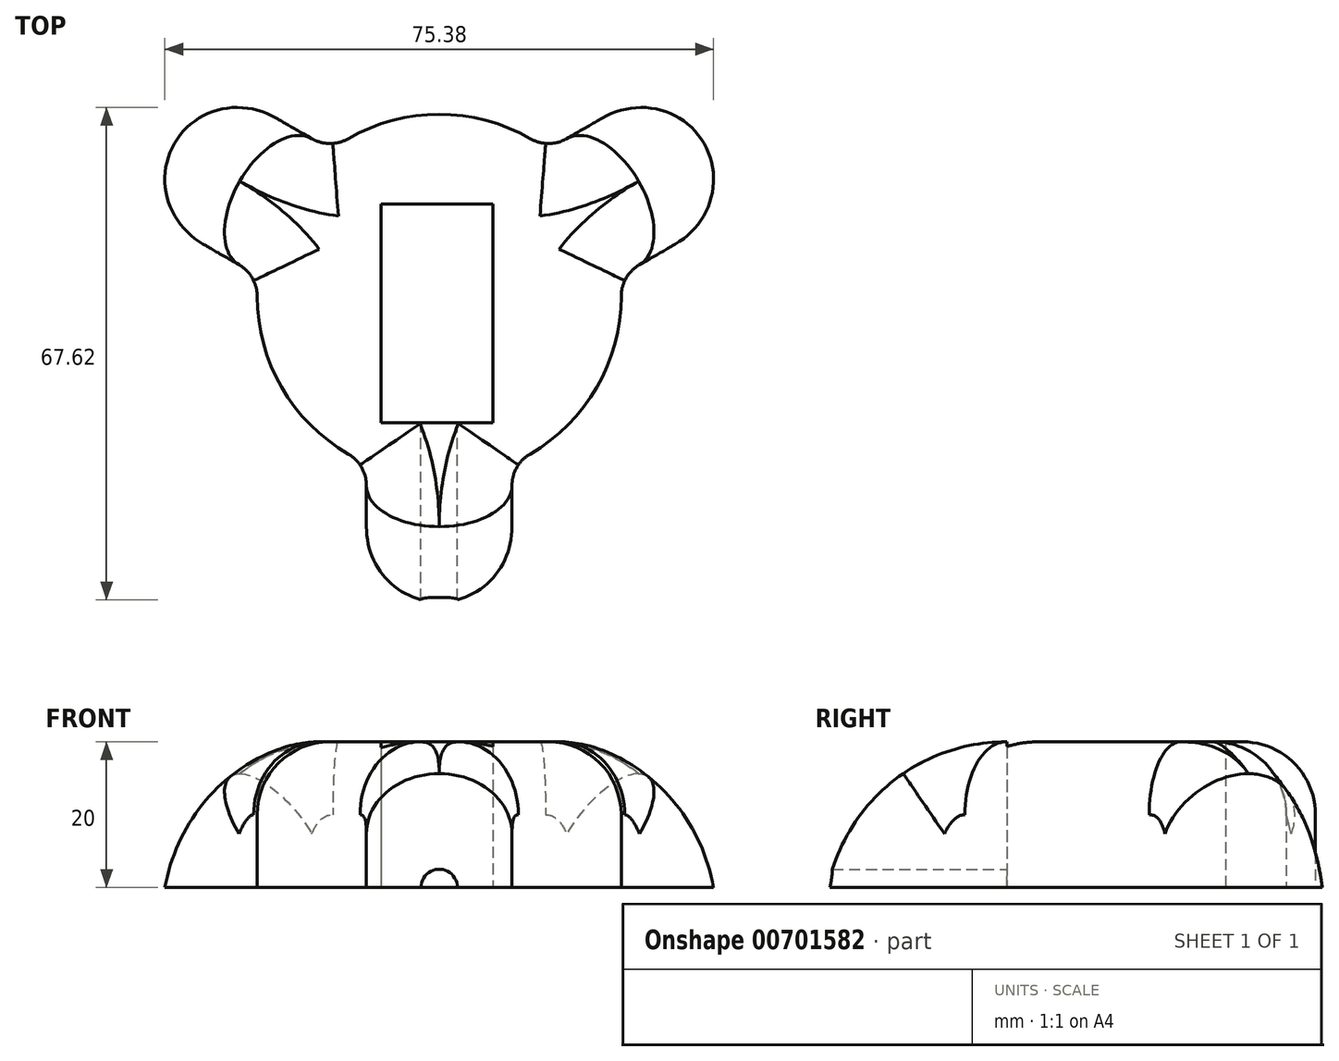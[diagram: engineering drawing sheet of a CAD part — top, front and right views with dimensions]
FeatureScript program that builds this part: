
annotation { "Feature Type Name" : "Feature", "Feature Type Description" : "" }
export const myFeature = defineFeature(function(context is Context, id is Id, definition is map)
    precondition{}
    {
        {
            var Q0;
            Q0=qCreatedBy(makeId("Top.planeOp"),FACE);
            var sketch = newSketch(context, id + "F0", { "sketchPlane" : qUnion([Q0])});
            skCircle(sketch, "E0", {"center": v(0, 0) * mm, "radius": 25 * mm});
            skSolve(sketch);
        }
        {
            var Q0;
            Q0=makeQuery(id+"F0.imprint","IMPRINT",FACE,{"disambiguationData":[TD([[makeQuery(id+"F0.imprint","IMPRINT",EDGE,{"derivedFrom":sQuery(id+"F0.wireOp",EDGE,"E0")}),1.0]])]});
            extrude(context, id + "F1", {"entities" : qUnion([Q0]), "depth" : 20 * mm, "offsetDistance" : 25 * mm});
        }
        {
            var Q0;
            Q0=qCreatedBy(makeId("Top.planeOp"),FACE);
            var sketch = newSketch(context, id + "F2", { "sketchPlane" : qUnion([Q0])});
            skLineSegment(sketch, "E1.bottom", {"start": v(-10, 0) * mm, "end": v(10, 0) * mm});
            skLineSegment(sketch, "E1.top", {"start": v(-10, -42) * mm, "end": v(10, -42) * mm});
            skLineSegment(sketch, "E1.left", {"start": v(-10, 0) * mm, "end": v(-10, -42) * mm});
            skLineSegment(sketch, "E1.right", {"start": v(10, 0) * mm, "end": v(10, -42) * mm});
            skSolve(sketch);
        }
        {
            var Q0;
            Q0=makeQuery(id+"F2.imprint","IMPRINT",FACE,{"disambiguationData":[TD([[makeQuery(id+"F2.imprint","IMPRINT",EDGE,{"derivedFrom":sQuery(id+"F2.wireOp",EDGE,"E1.bottom")}),-1.0]])]});
            extrude(context, id + "F3", {"entities" : qUnion([Q0]), "operationType" : NewBodyOperationType.ADD, "depth" : 20 * mm, "offsetDistance" : 25 * mm});
        }
        {
            var Q0;
            Q0=qCreatedBy(makeId("Right.planeOp"),FACE);
            var sketch = newSketch(context, id + "F4", { "sketchPlane" : qUnion([Q0])});
            skLineSegment(sketch, "E2", {"start": v(0, 74.5) * mm, "end": v(0, 0) * mm});
            skSolve(sketch);
        }
        {
            var Q0;
            Q0=makeQuery(id+"F1.opExtrude","SWEPT_BODY",BODY,{"disambiguationData":[OSD([sQuery(id+"F0.wireOp",EDGE,"E0")])]});
            var Q1;
            Q1=sQuery(id+"F4.wireOp",EDGE,"E2");
            circularPattern(context, id + "F5", {"entities" : qUnion([Q0]), "axis" : qUnion([Q1]), "angle" : 360 * degree, "instanceCount" : 3, "equalSpace" : true});
        }
        {
            var Q0;
            Q0=makeQuery(id+"F5.opPattern","COPY",BODY,{"derivedFrom":makeQuery(id+"F1.opExtrude","SWEPT_BODY",BODY,{"disambiguationData":[OSD([sQuery(id+"F0.wireOp",EDGE,"E0")])]}),"instanceName":"1"});
            var Q1;
            Q1=makeQuery(id+"F1.opExtrude","SWEPT_BODY",BODY,{"disambiguationData":[OSD([sQuery(id+"F0.wireOp",EDGE,"E0")])]});
            var Q2;
            Q2=makeQuery(id+"F5.opPattern","COPY",BODY,{"derivedFrom":makeQuery(id+"F1.opExtrude","SWEPT_BODY",BODY,{"disambiguationData":[OSD([sQuery(id+"F0.wireOp",EDGE,"E0")])]}),"instanceName":"2"});
            booleanBodies(context, id + "F6", {"operationType" : BooleanOperationType.UNION, "tools" : qUnion([Q0, Q1, Q2])});
        }
        {
            var Q0;
            Q0=makeQuery(id+"F3.opExtrude","CAP_EDGE",EDGE,{"disambiguationData":[OSD([sQuery(id+"F2.wireOp",EDGE,"E1.top")])],"isStart":false});
            var Q1;
            Q1=makeQuery(id+"F5.opPattern","COPY",EDGE,{"derivedFrom":makeQuery(id+"F3.opExtrude","CAP_EDGE",EDGE,{"disambiguationData":[OSD([sQuery(id+"F2.wireOp",EDGE,"E1.top")])],"isStart":false}),"instanceName":"1"});
            var Q2;
            Q2=makeQuery(id+"F5.opPattern","COPY",EDGE,{"derivedFrom":makeQuery(id+"F3.opExtrude","CAP_EDGE",EDGE,{"disambiguationData":[OSD([sQuery(id+"F2.wireOp",EDGE,"E1.top")])],"isStart":false}),"instanceName":"2"});
            fillet(context, id + "F7", {"entities" : qUnion([Q0, Q1, Q2]), "radius" : 25 * mm, "tangentPropagation" : true, "allowEdgeOverflow" : false});
        }
        {
            var Q0;
            Q0=makeQuery(id+"F5.opPattern","COPY",EDGE,{"derivedFrom":makeQuery(id+"F3.boolean.opBoolean","INTERSECT",EDGE,{"derivedFrom":[makeQuery(id+"F1.opExtrude","SWEPT_FACE",FACE,{"disambiguationData":[OSD([sQuery(id+"F0.wireOp",EDGE,"E0")])]}),makeQuery(id+"F3.opExtrude","SWEPT_FACE",FACE,{"disambiguationData":[OSD([sQuery(id+"F2.wireOp",EDGE,"E1.right")])]})]}),"instanceName":"1"});
            var Q1;
            {var subQ0=makeQuery(id+"F1.opExtrude","SWEPT_FACE",FACE,{"disambiguationData":[OSD([sQuery(id+"F0.wireOp",EDGE,"E0")])]});var subQ1=makeQuery(id+"F5.opPattern","COPY",FACE,{"derivedFrom":subQ0,"instanceName":"1"});Q1=makeQuery(id+"F6.opBoolean","INTERSECT",EDGE,{"disambiguationData":[topologyDisambiguationEdgeConnected([makeQuery(id+"F3.opExtrude","SWEPT_FACE",FACE,{"disambiguationData":[OSD([sQuery(id+"F2.wireOp",EDGE,"E1.left")])]})])],"derivedFrom":[subQ1,makeQuery(id+"F5.opPattern","COPY",FACE,{"derivedFrom":subQ0,"instanceName":"2"})]});}
            var Q2;
            Q2=makeQuery(id+"F5.opPattern","COPY",EDGE,{"derivedFrom":makeQuery(id+"F3.boolean.opBoolean","INTERSECT",EDGE,{"derivedFrom":[makeQuery(id+"F1.opExtrude","SWEPT_FACE",FACE,{"disambiguationData":[OSD([sQuery(id+"F0.wireOp",EDGE,"E0")])]}),makeQuery(id+"F3.opExtrude","SWEPT_FACE",FACE,{"disambiguationData":[OSD([sQuery(id+"F2.wireOp",EDGE,"E1.left")])]})]}),"instanceName":"1"});
            var Q3;
            {var subQ0=makeQuery(id+"F1.opExtrude","SWEPT_FACE",FACE,{"disambiguationData":[OSD([sQuery(id+"F0.wireOp",EDGE,"E0")])]});var subQ1=makeQuery(id+"F5.opPattern","COPY",FACE,{"derivedFrom":subQ0,"instanceName":"1"});Q3=makeQuery(id+"F6.opBoolean","INTERSECT",EDGE,{"disambiguationData":[topologyDisambiguationEdgeConnected([makeQuery(id+"F5.opPattern","COPY",FACE,{"derivedFrom":makeQuery(id+"F3.opExtrude","SWEPT_FACE",FACE,{"disambiguationData":[OSD([sQuery(id+"F2.wireOp",EDGE,"E1.right")])]}),"instanceName":"2"})])],"derivedFrom":[subQ0,subQ1]});}
            var Q4;
            {var subQ0=makeQuery(id+"F1.opExtrude","SWEPT_FACE",FACE,{"disambiguationData":[OSD([sQuery(id+"F0.wireOp",EDGE,"E0")])]});var subQ1=makeQuery(id+"F5.opPattern","COPY",FACE,{"derivedFrom":subQ0,"instanceName":"1"});Q4=makeQuery(id+"F6.opBoolean","INTERSECT",EDGE,{"disambiguationData":[topologyDisambiguationEdgeConnected([makeQuery(id+"F5.opPattern","COPY",FACE,{"derivedFrom":makeQuery(id+"F3.opExtrude","SWEPT_FACE",FACE,{"disambiguationData":[OSD([sQuery(id+"F2.wireOp",EDGE,"E1.left")])]}),"instanceName":"2"})])],"derivedFrom":[subQ0,subQ1]});}
            var Q5;
            {var subQ0=makeQuery(id+"F1.opExtrude","SWEPT_FACE",FACE,{"disambiguationData":[OSD([sQuery(id+"F0.wireOp",EDGE,"E0")])]});var subQ1=makeQuery(id+"F5.opPattern","COPY",FACE,{"derivedFrom":subQ0,"instanceName":"1"});Q5=makeQuery(id+"F6.opBoolean","INTERSECT",EDGE,{"disambiguationData":[topologyDisambiguationEdgeConnected([makeQuery(id+"F3.opExtrude","SWEPT_FACE",FACE,{"disambiguationData":[OSD([sQuery(id+"F2.wireOp",EDGE,"E1.right")])]})])],"derivedFrom":[subQ1,makeQuery(id+"F5.opPattern","COPY",FACE,{"derivedFrom":subQ0,"instanceName":"2"})]});}
            fillet(context, id + "F8", {"entities" : qUnion([Q0, Q1, Q2, Q3, Q4, Q5]), "radius" : 5 * mm, "tangentPropagation" : true, "allowEdgeOverflow" : false});
        }
        {
            var Q0;
            Q0=makeQuery(id+"F7.opFillet","BLEND_EDGE",EDGE,{"blendedFrom":[makeQuery(id+"F5.opPattern","COPY",EDGE,{"derivedFrom":makeQuery(id+"F3.opExtrude","CAP_EDGE",EDGE,{"disambiguationData":[OSD([sQuery(id+"F2.wireOp",EDGE,"E1.top")])],"isStart":false}),"instanceName":"1"}),makeQuery(id+"F5.opPattern","COPY",FACE,{"derivedFrom":makeQuery(id+"F3.opExtrude","SWEPT_FACE",FACE,{"disambiguationData":[OSD([sQuery(id+"F2.wireOp",EDGE,"E1.right")])]}),"instanceName":"1"})],"blendedInto":[makeQuery(id+"F5.opPattern","COPY",FACE,{"derivedFrom":makeQuery(id+"F3.opExtrude","SWEPT_FACE",FACE,{"disambiguationData":[OSD([sQuery(id+"F2.wireOp",EDGE,"E1.right")])]}),"instanceName":"1"})]});
            var Q1;
            {var subQ0=sQuery(id+"F2.wireOp",EDGE,"E1.top");var subQ1=makeQuery(id+"F1.opExtrude","SWEPT_FACE",FACE,{"disambiguationData":[OSD([sQuery(id+"F0.wireOp",EDGE,"E0")])]});var subQ2=makeQuery(id+"F5.opPattern","COPY",FACE,{"derivedFrom":subQ1,"instanceName":"1"});Q1=makeQuery(id+"F8.opFillet","BLEND_EDGE",EDGE,{"blendedFrom":[makeQuery(id+"F6.opBoolean","INTERSECT",EDGE,{"disambiguationData":[topologyDisambiguationEdgeConnected([makeQuery(id+"F5.opPattern","COPY",FACE,{"derivedFrom":makeQuery(id+"F3.opExtrude","SWEPT_FACE",FACE,{"disambiguationData":[OSD([sQuery(id+"F2.wireOp",EDGE,"E1.left")])]}),"instanceName":"2"})])],"derivedFrom":[subQ1,subQ2]}),makeQuery(id+"F7.opFillet","BLEND_FACE",FACE,{"disambiguationData":[OSD([subQ0]),TDD([makeQuery(id+"F5.opPattern","COPY",EDGE,{"derivedFrom":makeQuery(id+"F3.opExtrude","CAP_EDGE",EDGE,{"disambiguationData":[OSD([subQ0])],"isStart":false}),"instanceName":"2"})])]})],"blendedInto":[makeQuery(id+"F7.opFillet","BLEND_FACE",FACE,{"disambiguationData":[OSD([subQ0]),TDD([makeQuery(id+"F5.opPattern","COPY",EDGE,{"derivedFrom":makeQuery(id+"F3.opExtrude","CAP_EDGE",EDGE,{"disambiguationData":[OSD([subQ0])],"isStart":false}),"instanceName":"2"})])]})]});}
            var Q2;
            Q2=makeQuery(id+"F7.opFillet","BLEND_EDGE",EDGE,{"blendedFrom":[makeQuery(id+"F5.opPattern","COPY",EDGE,{"derivedFrom":makeQuery(id+"F3.opExtrude","CAP_EDGE",EDGE,{"disambiguationData":[OSD([sQuery(id+"F2.wireOp",EDGE,"E1.top")])],"isStart":false}),"instanceName":"2"}),makeQuery(id+"F5.opPattern","COPY",FACE,{"derivedFrom":makeQuery(id+"F3.opExtrude","SWEPT_FACE",FACE,{"disambiguationData":[OSD([sQuery(id+"F2.wireOp",EDGE,"E1.right")])]}),"instanceName":"2"})],"blendedInto":[makeQuery(id+"F5.opPattern","COPY",FACE,{"derivedFrom":makeQuery(id+"F3.opExtrude","SWEPT_FACE",FACE,{"disambiguationData":[OSD([sQuery(id+"F2.wireOp",EDGE,"E1.right")])]}),"instanceName":"2"})]});
            fillet(context, id + "F9", {"entities" : qUnion([Q0, Q1, Q2]), "radius" : 10 * mm, "tangentPropagation" : true, "allowEdgeOverflow" : false});
        }
        {
            var Q0;
            Q0=qCreatedBy(makeId("Front.planeOp"),FACE);
            var sketch = newSketch(context, id + "F10", { "sketchPlane" : qUnion([Q0])});
            skCircle(sketch, "E3", {"center": v(0, 0) * mm, "radius": 2.5 * mm});
            skSolve(sketch);
        }
        {
            var Q0;
            Q0=makeQuery(id+"F10.imprint","IMPRINT",FACE,{"disambiguationData":[TD([[makeQuery(id+"F10.imprint","IMPRINT",EDGE,{"derivedFrom":sQuery(id+"F10.wireOp",EDGE,"E3")}),1.0]])]});
            extrude(context, id + "F11", {"entities" : qUnion([Q0]), "operationType" : NewBodyOperationType.REMOVE, "depth" : 54.7 * mm, "offsetDistance" : 25 * mm});
        }
        {
            var Q0;
            {var subQ0=makeQuery(id+"F3.boolean.opBoolean","MERGE",FACE,{"derivedFrom":[makeQuery(id+"F1.opExtrude","CAP_FACE",FACE,{"disambiguationData":[OSD([sQuery(id+"F0.wireOp",EDGE,"E0")])],"isStart":true}),makeQuery(id+"F3.opExtrude","CAP_FACE",FACE,{"disambiguationData":[OSD([sQuery(id+"F2.wireOp",EDGE,"E1.bottom"),sQuery(id+"F2.wireOp",EDGE,"E1.top"),sQuery(id+"F2.wireOp",EDGE,"E1.left"),sQuery(id+"F2.wireOp",EDGE,"E1.right")])],"isStart":true})]});Q0=makeQuery(id+"F6.opBoolean","MERGE",FACE,{"derivedFrom":[subQ0,makeQuery(id+"F5.opPattern","COPY",FACE,{"derivedFrom":subQ0,"instanceName":"1"}),makeQuery(id+"F5.opPattern","COPY",FACE,{"derivedFrom":subQ0,"instanceName":"2"})]});}
            var sketch = newSketch(context, id + "F12", { "sketchPlane" : qUnion([Q0])});
            skLineSegment(sketch, "E4", {"start": v(0, 0) * mm, "end": v(0, 49.75) * mm});
            skSolve(sketch);
        }
        {
            var Q0;
            {var subQ3=sQuery(id+"F2.wireOp",EDGE,"E1.left");var subQ21=makeQuery(id+"F3.opExtrude","CAP_EDGE",EDGE,{"disambiguationData":[OSD([subQ3])],"isStart":true});Q0=makeQuery(id+"F12.imprint","IMPRINT",FACE,{"disambiguationData":[TD([[makeQuery(id+"F12.imprint","IMPRINT",EDGE,{"derivedFrom":subQ21}),-1.0]])]});}
            var sketch = newSketch(context, id + "F13", { "sketchPlane" : qUnion([Q0])});
            skLineSegment(sketch, "E5.bottom", {"start": v(7.37, 17.36) * mm, "end": v(-8, 17.36) * mm});
            skLineSegment(sketch, "E5.top", {"start": v(7.37, -12.65) * mm, "end": v(-8, -12.65) * mm});
            skLineSegment(sketch, "E5.left", {"start": v(7.37, 17.36) * mm, "end": v(7.37, -12.65) * mm});
            skLineSegment(sketch, "E5.right", {"start": v(-8, 17.36) * mm, "end": v(-8, -12.65) * mm});
            skSolve(sketch);
        }
        {
            var Q0;
            Q0 = qSketchRegion(id + "F13", true);
            extrude(context, id + "F14", {"entities" : qUnion([Q0]), "operationType" : NewBodyOperationType.REMOVE, "oppositeDirection" : true, "depth" : 29.8 * mm, "offsetDistance" : 25 * mm});
        }
    });
